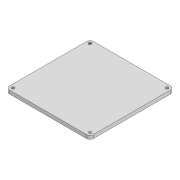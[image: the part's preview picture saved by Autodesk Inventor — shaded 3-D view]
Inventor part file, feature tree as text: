
AUTODESK INVENTOR PART (.ipt)
format: ipt  version: 2020 (Build 240168000, 168)  size: 103,424 bytes
history: native  units: mm
features: extrude x2, sketch x2, fillet x1
ambient origin geometry x8: Origin, YZ Plane, XZ Plane, XY Plane, X Axis, Y Axis, Z Axis, Center Point
bodies: Solid1 (feature_tree)
feature tree (5):
  extrude  "Extrusion1"  Depth=120.0mm
  extrude  "Extrusion2"  Depth=5.0mm
  fillet  "Fillet1"  Radius=110.0mm
  sketch  "Sketch1"  dims[d0=120.0mm d1=120.0mm]
  sketch  "Sketch2"  dims[d2=5.0mm d3=0.0mm d4=110.0mm d5=110.0mm d6=4.0mm d7=4.0mm d8=4.0mm d9=4.0mm d10=5.0mm d11=0.0mm d12=5.0mm]
